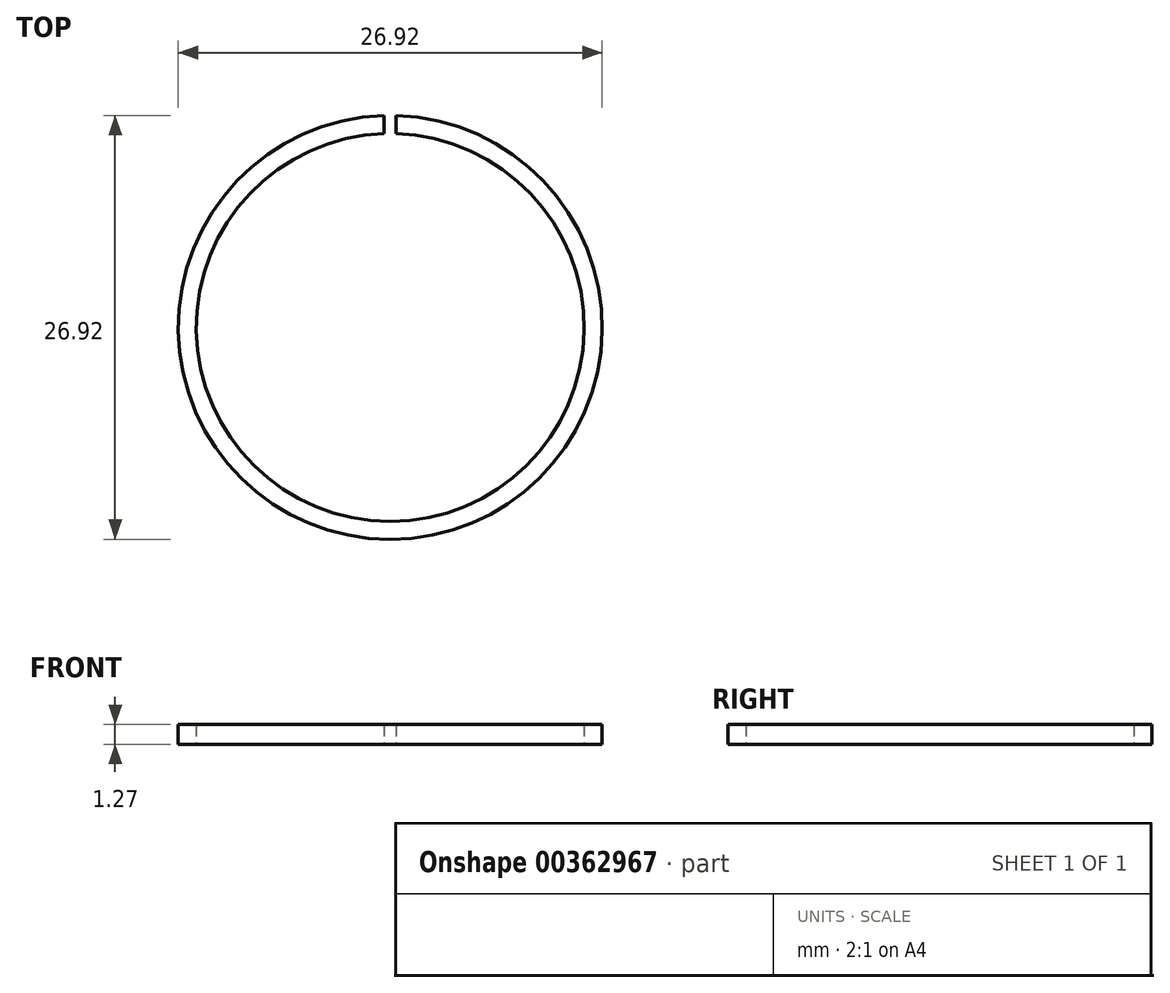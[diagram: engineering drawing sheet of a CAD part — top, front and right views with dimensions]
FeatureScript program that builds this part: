
annotation { "Feature Type Name" : "Feature", "Feature Type Description" : "" }
export const myFeature = defineFeature(function(context is Context, id is Id, definition is map)
    precondition{}
    {
        {
            var Q0;
            Q0=qCreatedBy(makeId("Top.planeOp"),FACE);
            var sketch = newSketch(context, id + "F0", { "sketchPlane" : qUnion([Q0])});
            skCircle(sketch, "E0", {"center": v(0, 0) * mm, "radius": 12.32 * mm});
            skCircle(sketch, "E1", {"center": v(0, 0) * mm, "radius": 13.46 * mm});
            skLineSegment(sketch, "E2.0", {"start": v(0.38, 0) * mm, "end": v(0.38, 15.77) * mm});
            skLineSegment(sketch, "E3.0", {"start": v(-0.38, 0) * mm, "end": v(-0.38, 15.77) * mm});
            skSolve(sketch);
        }
        {
            var Q0;
            {var subQ0=sQuery(id+"F0.wireOp",EDGE,"E2.0");var subQ1=sQuery(id+"F0.wireOp",EDGE,"E0");var subQ2=makeQuery(id+"F0.imprint","INTERSECT",VERTEX,{"derivedFrom":[subQ1,subQ0]});Q0=makeQuery(id+"F0.imprint","IMPRINT",FACE,{"disambiguationData":[TD([[makeQuery(id+"F0.imprint","IMPRINT",EDGE,{"disambiguationData":[TD([[subQ2,1.0]])],"derivedFrom":subQ1}),-1.0]])]});}
            extrude(context, id + "F1", {"entities" : qUnion([Q0]), "depth" : 1.27 * mm});
        }
    });
